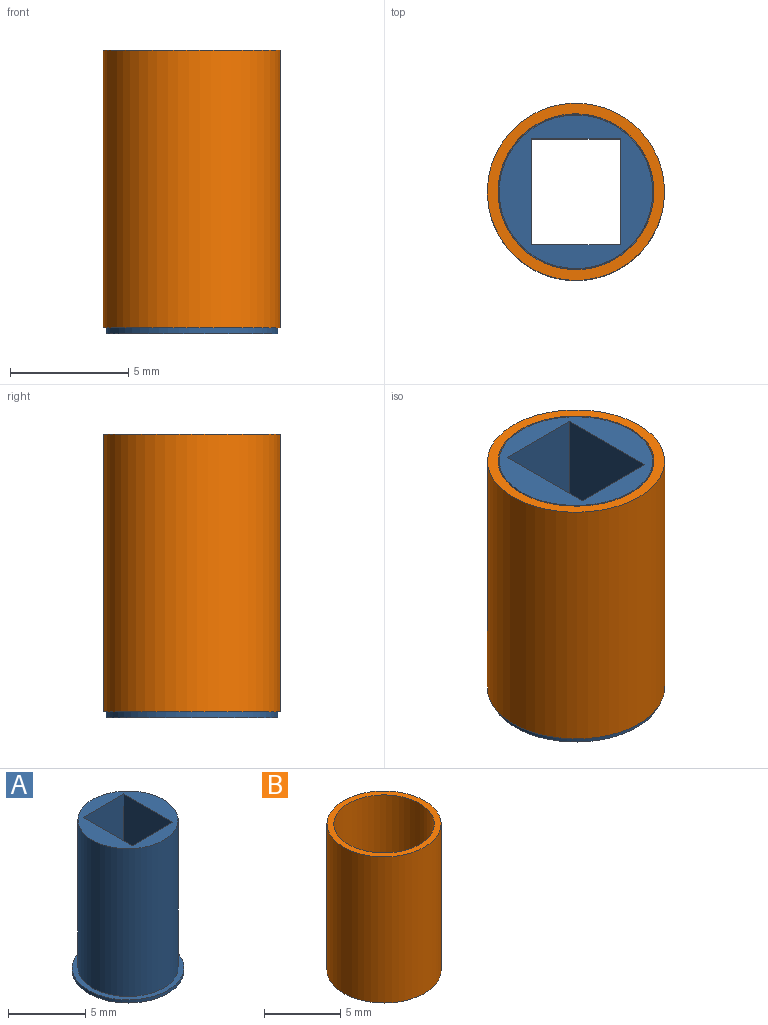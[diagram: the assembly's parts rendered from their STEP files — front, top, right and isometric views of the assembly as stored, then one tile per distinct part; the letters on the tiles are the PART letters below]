
ASSEMBLY  parts=2 mates=1
PART A: 9 faces, bbox 7.3x7.3x12 mm
  f0: plane 12x3.75mm, normal (0,1,0), area 45mm2, adj f1,f3,f5,f6
  f1: plane 12x4.5mm, normal (1,0,0), area 54mm2, adj f0,f2,f5,f6
  f2: plane 12x3.75mm, normal (0,-1,0), area 45mm2, adj f1,f3,f5,f6
  f3: plane 12x4.5mm, normal (-1,0,0), area 54mm2, adj f0,f2,f5,f6
  f4: cylinder r=3.25mm len=11.75mm, axis (0,0,-1), area 239.9mm2, adj f5,f8
  f5: plane 6.5x6.5mm, normal (0,0,1), area 16.3mm2, adj f0,f1,f2,f3,f4
  f6: plane 7.25x7.25mm, normal (0,0,-1), area 24.4mm2, adj f0,f1,f2,f3,f7
  f7: cylinder r=3.62mm len=7.25mm, axis (0,0,-1), area 5.7mm2, adj f6,f8
  f8: plane 7.25x7.25mm, normal (0,0,1), area 8.1mm2, adj f4,f7
PART B: 4 faces, bbox 7.5x7.5x11.8 mm
  f0: cylinder r=3.3mm len=11.75mm, axis (0,0,-1), area 243.6mm2, adj f2,f3
  f1: cylinder r=3.75mm len=11.75mm, axis (0,0,-1), area 276.9mm2, adj f2,f3
  f2: plane 7.5x7.5mm, normal (0,0,1), area 10mm2, adj f0,f1
  f3: plane 7.5x7.5mm, normal (0,0,-1), area 10mm2, adj f0,f1
PLACE A t=(-0.52,4.8,-0.33)mm
PLACE B t=(-0.52,4.8,-0.08)mm
MATE revolute A.f4 <-> B.f0  axis (0,0,-1) through (-0.52,4.8,5.79)mm
